# Revit family: Toilet_Tank-In_Wall-KOHLER-HYDRO_TOWER-K-6281T_1
name_source: partatom
category: Plumbing Fixtures
revit_build: Autodesk Revit 2017 (Build: 20160225_1515(x64)
units: mm (PartAtom-declared; Revit-internal decimal feet)

## family parameters
Cut with Voids When Loaded = No
Host = Face
OmniClass Number = 23.31.19.19.19
OmniClass Title = Water Closet Tanks
Part Type = Normal
Room Calculation Point = No
Round Connector Dimension = Use Diameter
Shared = No

## types (2) — shared parameters
ADA Compliant = No
Apparent Load = 0 VA
Assembly Code = D2010100
CW Connection = Yes
Cold Water Inlet = Cold Water Inlet
Cold Water Outlet = Cold Water Outlet
Date Modified = 01/05/2021
Default Elevation = 0"
Electrical Connector = Yes
Electrical Note = One Dedicated Circuit Required
Finish = Kohler-Metal-NA-Stainless
Flow Rate = 0 GPM
Flush Rate- GPF = 0 GPF
Flush Rate- LPF = 6 LPF
HW Connection = No
Hot Water Inlet = Hot Water Inlet
Length = 8 7/8"
Manufacturer = KOHLER Co.
Master Format 2014 = 22 41 13.13
Master Format 2014 Name = Residential Water Closets
Material = Premium Metal Construction
Pressure = 0.00 psi
Product Documentation Link = https://files.kohler.com.cn
Product Name = HYDRO TOWER
Seat Included = No
URL = http://www.kohler.com.cn
Vent Connection = No
Voltage = 220 V
Waste Connection = Yes
Waste Water Inlet = Waste Water Inlet
Waste Water Outlet = Waste Water Outlet
WaterSense Certified = No
Width = 18 13/16"

## per-type parameters (varying)
| type | Description | Model | Type |
| NA-Stainless Steel | 100 Touchless Inwall Tank With Frame | K-6281T-NA | 1 |
| W, NA-Stainless Steel | 3/ 4.5L HYDRO - TOWER 100 Touchless Inwall Tank With Frame | K-6281T-W-NA | 2 |

## geometry (parser evidence)
native form markers: Blend x5, Extrusion x1, Sweep x5
no freeform markers — native parametric forms only
